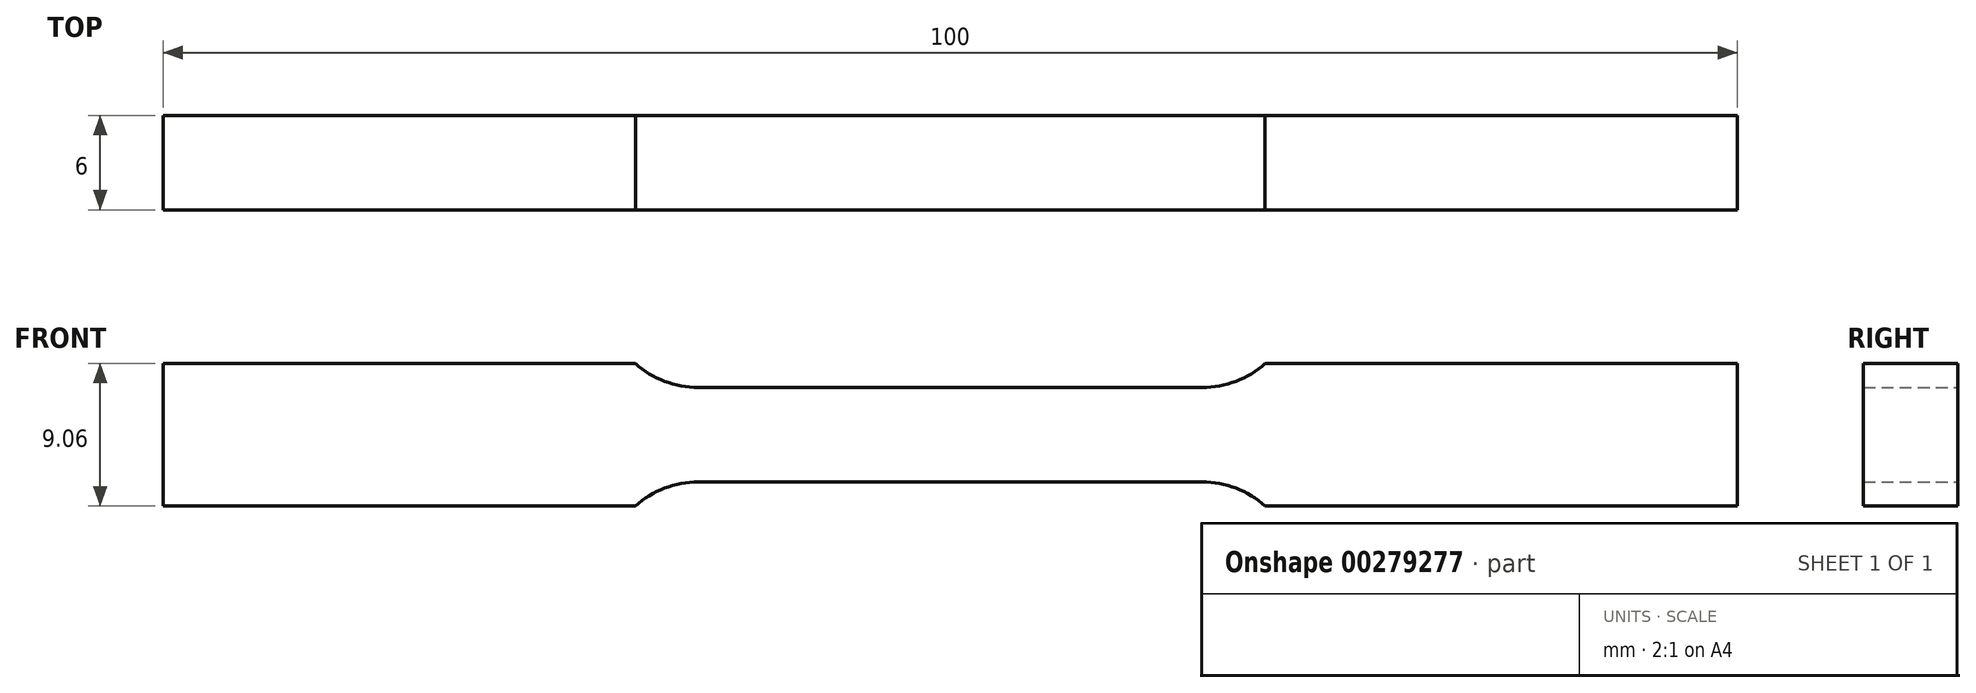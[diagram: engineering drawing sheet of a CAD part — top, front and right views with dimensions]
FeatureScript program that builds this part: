
annotation { "Feature Type Name" : "Feature", "Feature Type Description" : "" }
export const myFeature = defineFeature(function(context is Context, id is Id, definition is map)
    precondition{}
    {
        {
            var Q0;
            Q0=qCreatedBy(makeId("Front.planeOp"),FACE);
            var sketch = newSketch(context, id + "F0", { "sketchPlane" : qUnion([Q0])});
            skLineSegment(sketch, "E0", {"start": v(0, 3) * mm, "end": v(16, 3) * mm});
            skArc(sketch, "E1", {"start": v(16, 3) * mm, "mid": v(18.14, 3.4) * mm, "end": v(20, 4.53) * mm});
            skLineSegment(sketch, "E2", {"start": v(20, 4.53) * mm, "end": v(50, 4.53) * mm});
            skLineSegment(sketch, "E3", {"start": v(50, 4.53) * mm, "end": v(50, 0) * mm});
            skLineSegment(sketch, "E4.MirrorCS", {"start": v(0, -3) * mm, "end": v(16, -3) * mm});
            skLineSegment(sketch, "E5.MirrorCS", {"start": v(50, -4.53) * mm, "end": v(50, 0) * mm});
            skLineSegment(sketch, "E6.MirrorCS", {"start": v(20, -4.53) * mm, "end": v(50, -4.53) * mm});
            skArc(sketch, "E7.MirrorCS", {"start": v(16, -3) * mm, "mid": v(18.14, -3.4) * mm, "end": v(20, -4.53) * mm});
            skArc(sketch, "E8.MirrorCS", {"start": v(-16, -3) * mm, "mid": v(-18.14, -3.4) * mm, "end": v(-20, -4.53) * mm});
            skArc(sketch, "E9.MirrorCS", {"start": v(-16, 3) * mm, "mid": v(-18.14, 3.4) * mm, "end": v(-20, 4.53) * mm});
            skLineSegment(sketch, "E10.MirrorCS", {"start": v(-20, -4.53) * mm, "end": v(-50, -4.53) * mm});
            skLineSegment(sketch, "E11.MirrorCS", {"start": v(0, 3) * mm, "end": v(-16, 3) * mm});
            skLineSegment(sketch, "E12.MirrorCS", {"start": v(-20, 4.53) * mm, "end": v(-50, 4.53) * mm});
            skLineSegment(sketch, "E13.MirrorCS", {"start": v(-50, -4.53) * mm, "end": v(-50, 0) * mm});
            skLineSegment(sketch, "E14.MirrorCS", {"start": v(-50, 4.53) * mm, "end": v(-50, 0) * mm});
            skLineSegment(sketch, "E15.MirrorCS", {"start": v(0, -3) * mm, "end": v(-16, -3) * mm});
            skSolve(sketch);
        }
        {
            var Q0;
            Q0 = qSketchRegion(id + "F0", true);
            extrude(context, id + "F1", {"entities" : qUnion([Q0]), "endBound" : BoundingType.SYMMETRIC, "depth" : 6 * mm});
        }
    });
